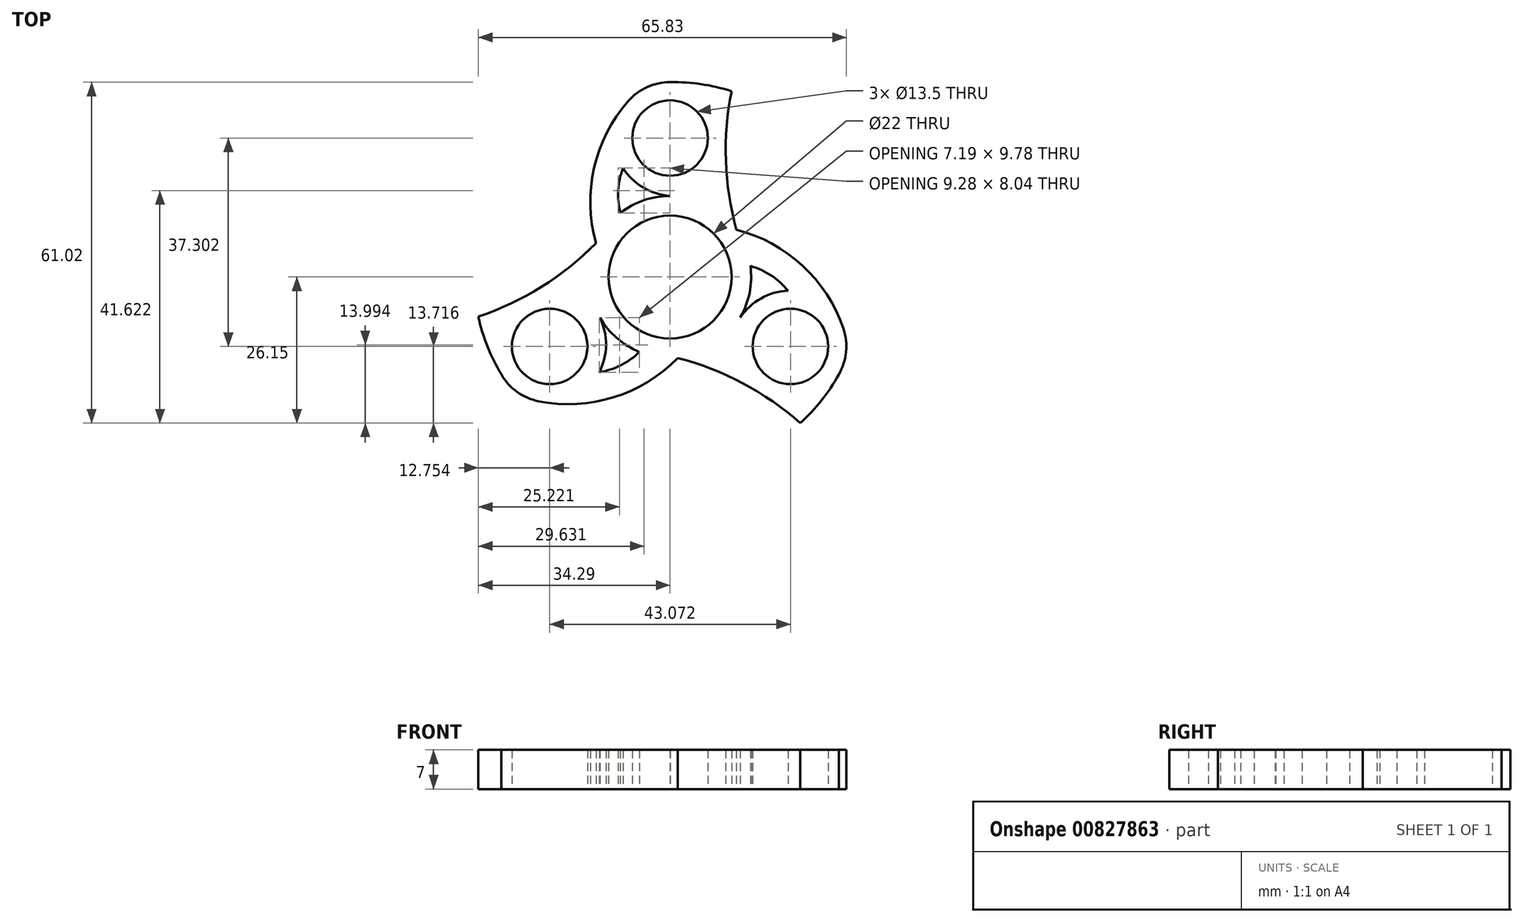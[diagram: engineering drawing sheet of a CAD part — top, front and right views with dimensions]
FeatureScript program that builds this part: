
annotation { "Feature Type Name" : "Feature", "Feature Type Description" : "" }
export const myFeature = defineFeature(function(context is Context, id is Id, definition is map)
    precondition{}
    {
        {
            var Q0;
            Q0=qCreatedBy(makeId("Top.planeOp"),FACE);
            var sketch = newSketch(context, id + "F0", { "sketchPlane" : qUnion([Q0])});
            skCircle(sketch, "E0", {"center": v(0, 0) * mm, "radius": 11 * mm});
            skArc(sketch, "E1", {"start": v(-0.02, 14.5) * mm, "mid": v(-4.7, 13.71) * mm, "end": v(-8.9, 11.45) * mm});
            skCircle(sketch, "E2", {"center": v(0, 24.87) * mm, "radius": 6.75 * mm});
            skArc(sketch, "E3", {"start": v(-7.52, 31.46) * mm, "mid": v(-13.62, 19.44) * mm, "end": v(-13.21, 5.97) * mm});
            skArc(sketch, "E4", {"start": v(11, 33.25) * mm, "mid": v(5.54, 34.46) * mm, "end": v(-0.03, 34.87) * mm, "construction": true});
            skLineSegment(sketch, "E5", {"start": v(9.18, 40.3) * mm, "end": v(9.18, 40.3) * mm});
            skArc(sketch, "E6", {"start": v(11, 33.25) * mm, "mid": v(9.98, 20.7) * mm, "end": v(11.92, 8.26) * mm});
            skArc(sketch, "E7", {"start": v(11, 33.25) * mm, "mid": v(5.58, 34.5) * mm, "end": v(0.03, 34.87) * mm});
            skPoint(sketch, "E8", {"position": v(9.96, 23.97) * mm});
            skArc(sketch, "E9", {"start": v(-8.43, 19.49) * mm, "mid": v(-9.28, 15.5) * mm, "end": v(-8.9, 11.45) * mm});
            skArc(sketch, "E10", {"start": v(-8.43, 19.49) * mm, "mid": v(-4.8, 16.01) * mm, "end": v(-0.02, 14.5) * mm});
            skArc(sketch, "E11.trimOffspring", {"start": v(-12.55, -7.27) * mm, "mid": v(-9.52, -10.93) * mm, "end": v(-5.47, -13.43) * mm});
            skArc(sketch, "E12.trimOffspring", {"start": v(0.03, 34.87) * mm, "mid": v(-4.11, 33.98) * mm, "end": v(-7.52, 31.46) * mm});
            skArc(sketch, "E13.1.0", {"start": v(-23.49, -22.24) * mm, "mid": v(-10.03, -21.52) * mm, "end": v(1.44, -14.43) * mm});
            skArc(sketch, "E13.1.1", {"start": v(-12.66, -17.05) * mm, "mid": v(-8.8, -15.79) * mm, "end": v(-5.47, -13.43) * mm});
            skArc(sketch, "E13.1.2", {"start": v(-12.66, -17.05) * mm, "mid": v(-11.46, -12.17) * mm, "end": v(-12.55, -7.27) * mm});
            skCircle(sketch, "E13.1.3", {"center": v(-21.54, -12.43) * mm, "radius": 6.75 * mm});
            skArc(sketch, "E13.1.4", {"start": v(-30.21, -17.4) * mm, "mid": v(-27.37, -20.55) * mm, "end": v(-23.49, -22.24) * mm});
            skArc(sketch, "E13.1.5", {"start": v(-34.3, -7.1) * mm, "mid": v(-22.92, -1.7) * mm, "end": v(-13.11, 6.2) * mm});
            skArc(sketch, "E13.1.6", {"start": v(-34.3, -7.1) * mm, "mid": v(-32.67, -12.42) * mm, "end": v(-30.21, -17.4) * mm});
            skArc(sketch, "E13.2.0", {"start": v(31, -9.22) * mm, "mid": v(23.65, 2.08) * mm, "end": v(11.78, 8.46) * mm});
            skArc(sketch, "E13.2.1", {"start": v(21.1, -2.44) * mm, "mid": v(18.07, 0.28) * mm, "end": v(14.37, 1.97) * mm});
            skArc(sketch, "E13.2.2", {"start": v(21.1, -2.44) * mm, "mid": v(16.27, -3.84) * mm, "end": v(12.57, -7.23) * mm});
            skCircle(sketch, "E13.2.3", {"center": v(21.54, -12.43) * mm, "radius": 6.75 * mm});
            skArc(sketch, "E13.2.4", {"start": v(30.18, -17.46) * mm, "mid": v(31.49, -13.43) * mm, "end": v(31, -9.22) * mm});
            skArc(sketch, "E13.2.5", {"start": v(23.3, -26.15) * mm, "mid": v(12.94, -19) * mm, "end": v(1.2, -14.45) * mm});
            skArc(sketch, "E13.2.6", {"start": v(23.3, -26.15) * mm, "mid": v(27.1, -22.08) * mm, "end": v(30.18, -17.46) * mm});
            skArc(sketch, "E14.trimOffspring", {"start": v(1.2, -14.45) * mm, "mid": v(1.32, -14.44) * mm, "end": v(1.44, -14.43) * mm});
            skArc(sketch, "E15.trimOffspring", {"start": v(12.57, -7.23) * mm, "mid": v(14.23, -2.78) * mm, "end": v(14.37, 1.97) * mm});
            skSolve(sketch);
        }
        {
            var Q0;
            Q0 = qSketchRegion(id + "F0", true);
            extrude(context, id + "F1", {"entities" : qUnion([Q0]), "depth" : 7 * mm, "offsetDistance" : 25 * mm});
        }
    });
